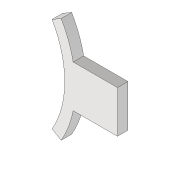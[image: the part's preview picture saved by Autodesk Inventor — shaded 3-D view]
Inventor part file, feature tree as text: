
AUTODESK INVENTOR PART (.ipt)
format: ipt  version: 2020 (Build 240168000, 168)  size: 164,352 bytes
history: native  units: mm
features: extrude x5, sketch x5, projected_geometry x2
ambient origin geometry x8: Origin, YZ Plane, XZ Plane, XY Plane, X Axis, Y Axis, Z Axis, Center Point
bodies: Volumenkörper1 (feature_tree)
feature tree (12):
  extrude  "Extrusion1"  Depth=20.0mm
  extrude  "Extrusion3"  Depth=5.0mm
  extrude  "Extrusion4"  TaperAngle=90.0deg  [1 undecoded]
  extrude  "Extrusion5"  Depth=10.0mm TaperAngle=0.0deg
  extrude  "Extrusion6"  Depth=10.0mm
  sketch  "Skizze1"  dims[d0=30.0mm d1=20.0mm]
  sketch  "Skizze3"  dims[d2=5.0mm d3=5.0mm]
  sketch  "Skizze4"  dims[d4=20.0mm d5=90.0deg]
  sketch  "Skizze5"  dims[d6=40.0mm d7=10.0mm d8=0.0mm]
  sketch  "Skizze6"  dims[d12=10.0mm d13=10.0mm d14=10.0mm d15=60.0mm d16=50.0mm d17=60.0mm d18=17.75mm d19=0.0mm d20=200.0mm d21=180.0mm d22=30.0deg d23=30.0deg d24=40.0mm d25=20.0mm d26=15.25mm d27=0.0mm d28=20.25mm d29=0.0mm d30=140.0mm d31=70.0mm d32=0.0mm]
  projected_geometry  "Projizierte Kontur1"
  projected_geometry  "Projizierte Kontur2"
note: 1 required parameter value undecoded (feature->parameter linkage not recoverable at this tier; creation-order binding heuristic only, values carry confidence <= 0.55)
